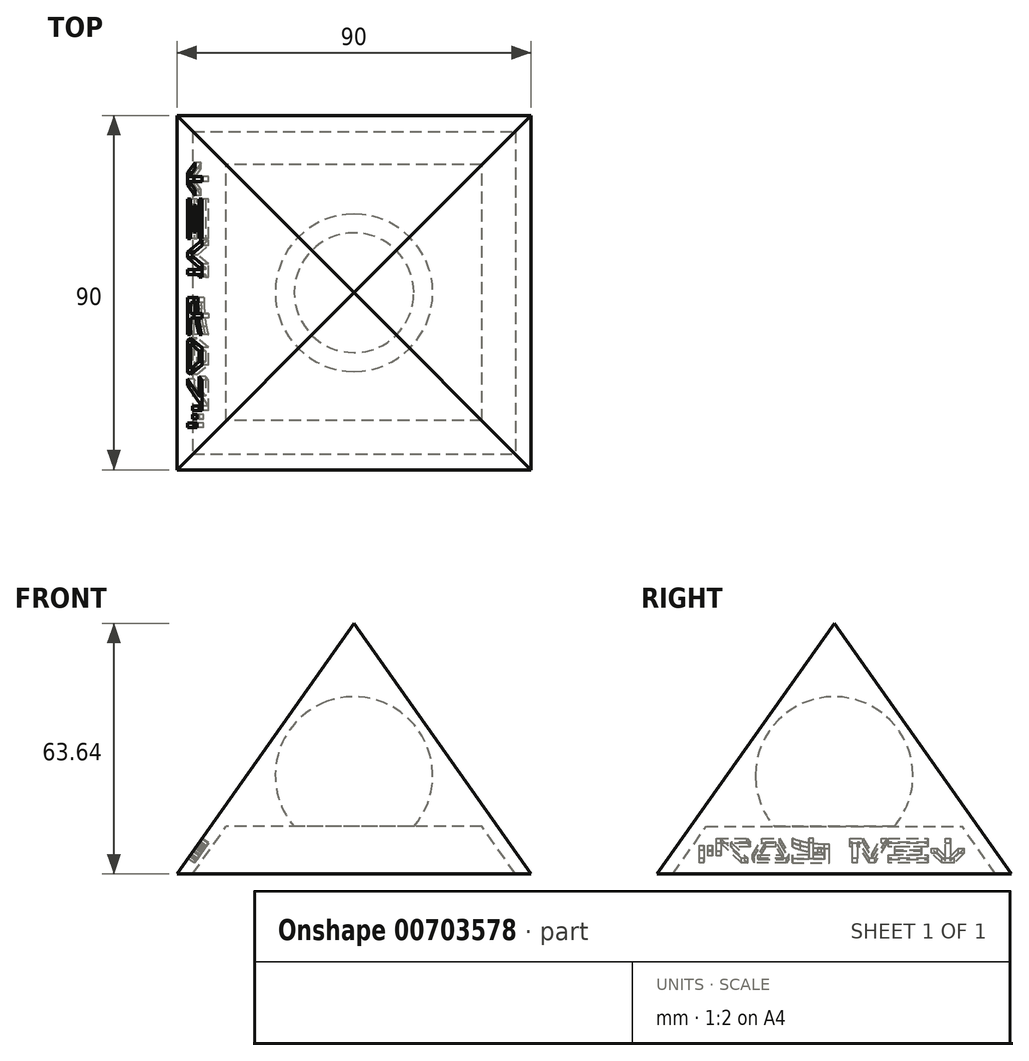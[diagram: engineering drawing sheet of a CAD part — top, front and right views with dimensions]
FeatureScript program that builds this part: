
annotation { "Feature Type Name" : "Feature", "Feature Type Description" : "" }
export const myFeature = defineFeature(function(context is Context, id is Id, definition is map)
    precondition{}
    {
        {
            var Q0;
            Q0=qCreatedBy(makeId("Top.planeOp"),FACE);
            cPlane(context, id + "F0", {"entities" : qUnion([Q0]), "cplaneType" : CPlaneType.OFFSET, "offset" : 63.64 * mm, "width" : 150 * mm, "height" : 150 * mm});
        }
        {
            var Q0;
            Q0=qCreatedBy(id+"F0.planeOp",FACE);
            var sketch = newSketch(context, id + "F1", { "sketchPlane" : qUnion([Q0])});
            skPoint(sketch, "E0", {"position": v(0, 0) * mm});
            skLineSegment(sketch, "E1.bottom", {"start": v(-47.05, 40.97) * mm, "end": v(62.4, 40.97) * mm});
            skLineSegment(sketch, "E1.top", {"start": v(-47.05, -49.65) * mm, "end": v(62.4, -49.65) * mm});
            skLineSegment(sketch, "E1.left", {"start": v(-47.05, 40.97) * mm, "end": v(-47.05, -49.65) * mm});
            skLineSegment(sketch, "E1.right", {"start": v(62.4, 40.97) * mm, "end": v(62.4, -49.65) * mm});
            skSolve(sketch);
        }
        {
            var Q0;
            Q0=qCreatedBy(makeId("Top.planeOp"),FACE);
            var sketch = newSketch(context, id + "F2", { "sketchPlane" : qUnion([Q0])});
            skLineSegment(sketch, "E2.bottom", {"start": v(-45, 45) * mm, "end": v(45, 45) * mm});
            skLineSegment(sketch, "E2.top", {"start": v(-45, -45) * mm, "end": v(45, -45) * mm});
            skLineSegment(sketch, "E2.left", {"start": v(-45, 45) * mm, "end": v(-45, -45) * mm});
            skLineSegment(sketch, "E2.right", {"start": v(45, 45) * mm, "end": v(45, -45) * mm});
            skPoint(sketch, "E3.orphan", {"position": v(-45, 0) * mm});
            skPoint(sketch, "E4.start.orphan", {"position": v(45, 0) * mm});
            skPoint(sketch, "E5.end.orphan", {"position": v(0, -45) * mm});
            skPoint(sketch, "E5.start.orphan", {"position": v(0, 45) * mm});
            skSolve(sketch);
        }
        {
            var Q0;
            Q0=makeQuery(id+"F2.imprint","IMPRINT",FACE,{"disambiguationData":[TD([[makeQuery(id+"F2.imprint","IMPRINT",EDGE,{"derivedFrom":sQuery(id+"F2.wireOp",EDGE,"E2.bottom")}),-1.0]])]});
            var Q1;
            Q1=sQuery(id+"F1.wireOp",VERTEX,"E0");
            loft(context, id + "F3", {"sheetProfilesArray" : [{ "sheetProfileEntities" : qUnion([Q0]) }, { "sheetProfileEntities" : qUnion([Q1]) }]});
        }
        {
            var Q0;
            Q0=qCreatedBy(makeId("Top.planeOp"),FACE);
            cPlane(context, id + "F4", {"entities" : qUnion([Q0]), "cplaneType" : CPlaneType.OFFSET, "offset" : 25 * mm, "width" : 150 * mm, "height" : 150 * mm});
        }
        {
            var Q0;
            Q0=qCreatedBy(makeId("Top.planeOp"),FACE);
            cPlane(context, id + "F5", {"entities" : qUnion([Q0]), "cplaneType" : CPlaneType.OFFSET, "offset" : 58 * mm, "width" : 150 * mm, "height" : 150 * mm});
        }
        {
            var Q0;
            Q0=qCreatedBy(id+"F5.planeOp",FACE);
            var sketch = newSketch(context, id + "F6", { "sketchPlane" : qUnion([Q0])});
            skPoint(sketch, "E6", {"position": v(0, 0) * mm});
            skSolve(sketch);
        }
        {
            var Q0;
            Q0=makeQuery(id+"F2.imprint","IMPRINT",FACE,{"disambiguationData":[TD([[makeQuery(id+"F2.imprint","IMPRINT",EDGE,{"derivedFrom":sQuery(id+"F2.wireOp",EDGE,"E2.bottom")}),-1.0]])]});
            var sketch = newSketch(context, id + "F7", { "sketchPlane" : qUnion([Q0])});
            skLineSegment(sketch, "E7.0", {"start": v(-41, 41) * mm, "end": v(-41, -41) * mm});
            skLineSegment(sketch, "E7.1", {"start": v(-41, 41) * mm, "end": v(41, 41) * mm});
            skLineSegment(sketch, "E7.2", {"start": v(41, 41) * mm, "end": v(41, -41) * mm});
            skLineSegment(sketch, "E7.3", {"start": v(-41, -41) * mm, "end": v(41, -41) * mm});
            skSolve(sketch);
        }
        {
            var Q1;
            Q1=makeQuery(id+"F7.imprint","IMPRINT",FACE,{"disambiguationData":[TD([[makeQuery(id+"F7.imprint","IMPRINT",EDGE,{"derivedFrom":sQuery(id+"F7.wireOp",EDGE,"E7.0")}),1.0]])]});
            var Q2;
            Q2=sQuery(id+"F6.wireOp",VERTEX,"E6");
            loft(context, id + "F8", {"operationType" : NewBodyOperationType.REMOVE, "sheetProfilesArray" : [{ "sheetProfileEntities" : qUnion([Q1]) }, { "sheetProfileEntities" : qUnion([Q2]) }]});
        }
        {
            var Q0;
            Q0=makeQuery(id+"F3.opLoft","SWEPT_FACE",FACE,{"disambiguationData":[OSD([sQuery(id+"F2.wireOp",EDGE,"E2.bottom"),sQuery(id+"F2.wireOp",EDGE,"E2.top"),sQuery(id+"F2.wireOp",EDGE,"E2.left")])]});
            var sketch = newSketch(context, id + "F9", { "sketchPlane" : qUnion([Q0])});
            skLineSegment(sketch, "E8", {"start": v(-30.48, -21.2) * mm, "end": v(-27.31, -21.2) * mm});
            skLineSegment(sketch, "E9", {"start": v(-27.31, -21.2) * mm, "end": v(-24.66, -18.07) * mm});
            skLineSegment(sketch, "E10", {"start": v(-24.66, -18.07) * mm, "end": v(-26.25, -18.07) * mm});
            skLineSegment(sketch, "E11", {"start": v(-26.25, -18.07) * mm, "end": v(-28.3, -20.5) * mm});
            skLineSegment(sketch, "E12", {"start": v(-28.3, -20.5) * mm, "end": v(-28.3, -14.95) * mm});
            skLineSegment(sketch, "E13", {"start": v(-28.3, -14.95) * mm, "end": v(-29.48, -14.95) * mm});
            skLineSegment(sketch, "E14", {"start": v(-29.48, -14.95) * mm, "end": v(-29.48, -20.5) * mm});
            skLineSegment(sketch, "E15", {"start": v(-29.48, -20.5) * mm, "end": v(-31.54, -18.07) * mm});
            skLineSegment(sketch, "E16", {"start": v(-31.54, -18.07) * mm, "end": v(-33.13, -18.07) * mm});
            skLineSegment(sketch, "E17", {"start": v(-33.13, -18.07) * mm, "end": v(-30.48, -21.2) * mm});
            skLineSegment(sketch, "E18", {"start": v(-13.74, -16.13) * mm, "end": v(-13.74, -14.95) * mm});
            skLineSegment(sketch, "E19", {"start": v(-13.74, -14.95) * mm, "end": v(-23.85, -14.95) * mm});
            skLineSegment(sketch, "E20", {"start": v(-23.85, -14.95) * mm, "end": v(-23.85, -16.13) * mm});
            skLineSegment(sketch, "E21", {"start": v(-23.85, -16.13) * mm, "end": v(-13.74, -16.13) * mm});
            skLineSegment(sketch, "E22", {"start": v(-13.74, -21.2) * mm, "end": v(-13.74, -20.01) * mm});
            skLineSegment(sketch, "E23", {"start": v(-13.74, -20.01) * mm, "end": v(-23.85, -20.01) * mm});
            skLineSegment(sketch, "E24", {"start": v(-23.85, -20.01) * mm, "end": v(-23.85, -21.2) * mm});
            skLineSegment(sketch, "E25", {"start": v(-23.85, -21.2) * mm, "end": v(-13.74, -21.2) * mm});
            skLineSegment(sketch, "E26", {"start": v(-15.46, -18.66) * mm, "end": v(-15.46, -17.48) * mm});
            skLineSegment(sketch, "E27", {"start": v(-15.46, -17.48) * mm, "end": v(-22.13, -17.48) * mm});
            skLineSegment(sketch, "E28", {"start": v(-22.13, -17.48) * mm, "end": v(-22.13, -18.66) * mm});
            skLineSegment(sketch, "E29", {"start": v(-22.13, -18.66) * mm, "end": v(-15.46, -18.66) * mm});
            skLineSegment(sketch, "E30", {"start": v(-9.62, -19.72) * mm, "end": v(-11.96, -14.95) * mm});
            skLineSegment(sketch, "E31", {"start": v(-11.96, -14.95) * mm, "end": v(-13.4, -14.95) * mm});
            skLineSegment(sketch, "E32", {"start": v(-13.4, -14.95) * mm, "end": v(-10.33, -21.2) * mm});
            skLineSegment(sketch, "E33", {"start": v(-10.33, -21.2) * mm, "end": v(-8.9, -21.2) * mm});
            skLineSegment(sketch, "E34", {"start": v(-8.9, -21.2) * mm, "end": v(-6.42, -16.13) * mm});
            skLineSegment(sketch, "E35", {"start": v(-6.42, -16.13) * mm, "end": v(-5.84, -16.13) * mm});
            skLineSegment(sketch, "E36", {"start": v(-5.84, -16.13) * mm, "end": v(-5.84, -21.2) * mm});
            skLineSegment(sketch, "E37", {"start": v(-5.84, -21.2) * mm, "end": v(-4.66, -21.2) * mm});
            skLineSegment(sketch, "E38", {"start": v(-4.66, -21.2) * mm, "end": v(-4.66, -16.13) * mm});
            skLineSegment(sketch, "E39", {"start": v(-4.66, -16.13) * mm, "end": v(-3.94, -16.13) * mm});
            skLineSegment(sketch, "E40", {"start": v(-3.94, -16.13) * mm, "end": v(-3.94, -14.95) * mm});
            skLineSegment(sketch, "E41", {"start": v(-3.94, -14.95) * mm, "end": v(-7.28, -14.95) * mm});
            skLineSegment(sketch, "E42", {"start": v(-7.28, -14.95) * mm, "end": v(-9.62, -19.72) * mm});
            skLineSegment(sketch, "E43", {"start": v(2.43, -20.01) * mm, "end": v(5.3, -20.01) * mm});
            skLineSegment(sketch, "E44", {"start": v(5.3, -20.01) * mm, "end": v(5.3, -17.82) * mm});
            skLineSegment(sketch, "E45", {"start": v(2.43, -17.95) * mm, "end": v(2.43, -20.01) * mm});
            skLineSegment(sketch, "E46", {"start": v(5.3, -16.6) * mm, "end": v(5.3, -14.95) * mm});
            skLineSegment(sketch, "E47", {"start": v(5.3, -14.95) * mm, "end": v(6.48, -14.95) * mm});
            skLineSegment(sketch, "E48", {"start": v(6.48, -14.95) * mm, "end": v(6.48, -16.4) * mm});
            skLineSegment(sketch, "E49", {"start": v(10.66, -14.95) * mm, "end": v(10.66, -16.14) * mm});
            skLineSegment(sketch, "E50", {"start": v(6.48, -17.65) * mm, "end": v(6.48, -20.01) * mm});
            skLineSegment(sketch, "E51", {"start": v(6.48, -20.01) * mm, "end": v(10.66, -20.01) * mm});
            skLineSegment(sketch, "E52", {"start": v(10.66, -20.01) * mm, "end": v(10.66, -21.2) * mm});
            skLineSegment(sketch, "E53", {"start": v(10.66, -21.2) * mm, "end": v(1.25, -21.2) * mm});
            skLineSegment(sketch, "E54", {"start": v(1.25, -21.2) * mm, "end": v(1.25, -16.76) * mm});
            skLineSegment(sketch, "E55", {"start": v(1.25, -16.76) * mm, "end": v(2.43, -16.76) * mm});
            skLineSegment(sketch, "E56", {"start": v(12.92, -20.01) * mm, "end": v(14.82, -16.13) * mm});
            skLineSegment(sketch, "E57", {"start": v(14.82, -16.13) * mm, "end": v(17.48, -16.13) * mm});
            skLineSegment(sketch, "E58", {"start": v(17.48, -16.13) * mm, "end": v(19.37, -20.01) * mm});
            skLineSegment(sketch, "E59", {"start": v(19.37, -20.01) * mm, "end": v(12.92, -20.01) * mm});
            skLineSegment(sketch, "E60", {"start": v(20.26, -21.2) * mm, "end": v(20.83, -20.04) * mm});
            skLineSegment(sketch, "E61", {"start": v(20.83, -20.04) * mm, "end": v(18.33, -14.95) * mm});
            skLineSegment(sketch, "E62", {"start": v(18.33, -14.95) * mm, "end": v(13.96, -14.95) * mm});
            skLineSegment(sketch, "E63", {"start": v(13.96, -14.95) * mm, "end": v(11.5, -19.98) * mm});
            skLineSegment(sketch, "E64", {"start": v(11.5, -19.98) * mm, "end": v(12.09, -21.2) * mm});
            skLineSegment(sketch, "E65", {"start": v(12.09, -21.2) * mm, "end": v(20.26, -21.2) * mm});
            skLineSegment(sketch, "E66", {"start": v(23.56, -21.2) * mm, "end": v(28.74, -15.1) * mm});
            skLineSegment(sketch, "E67", {"start": v(28.86, -14.95) * mm, "end": v(22.22, -14.95) * mm});
            skLineSegment(sketch, "E68", {"start": v(22.22, -14.95) * mm, "end": v(21.22, -16.13) * mm});
            skLineSegment(sketch, "E69", {"start": v(21.22, -16.13) * mm, "end": v(26.26, -16.13) * mm});
            skLineSegment(sketch, "E70", {"start": v(26.26, -16.13) * mm, "end": v(21.97, -21.2) * mm});
            skLineSegment(sketch, "E71", {"start": v(21.97, -21.2) * mm, "end": v(23.56, -21.2) * mm});
            skLineSegment(sketch, "E72", {"start": v(29.92, -19) * mm, "end": v(29.92, -14.95) * mm});
            skLineSegment(sketch, "E73", {"start": v(29.92, -14.95) * mm, "end": v(28.74, -14.95) * mm});
            skLineSegment(sketch, "E74", {"start": v(28.74, -15.1) * mm, "end": v(28.74, -19) * mm});
            skLineSegment(sketch, "E75", {"start": v(28.74, -19) * mm, "end": v(29.92, -19) * mm});
            skLineSegment(sketch, "E76", {"start": v(34.22, -21.2) * mm, "end": v(34.22, -17.13) * mm});
            skLineSegment(sketch, "E77", {"start": v(34.22, -17.13) * mm, "end": v(33.04, -17.13) * mm});
            skLineSegment(sketch, "E78", {"start": v(33.04, -17.13) * mm, "end": v(33.04, -21.2) * mm});
            skLineSegment(sketch, "E79", {"start": v(33.04, -21.2) * mm, "end": v(34.22, -21.2) * mm});
            skLineSegment(sketch, "E80", {"start": v(32.07, -19) * mm, "end": v(32.07, -17.13) * mm});
            skLineSegment(sketch, "E81", {"start": v(32.07, -17.13) * mm, "end": v(30.89, -17.13) * mm});
            skLineSegment(sketch, "E82", {"start": v(30.89, -17.13) * mm, "end": v(30.89, -19) * mm});
            skLineSegment(sketch, "E83", {"start": v(30.89, -19) * mm, "end": v(32.07, -19) * mm});
            skFitSpline(sketch, "E84", {"points": [v(5.3, -17.82) * mm, v(5.1, -17.85) * mm, v(4.72, -17.9) * mm, v(4.34, -17.92) * mm, v(4.16, -17.93) * mm]});
            skFitSpline(sketch, "E85", {"points": [v(4.16, -17.93) * mm, v(4, -17.94) * mm, v(3.7, -17.95) * mm, v(3.4, -17.96) * mm, v(3.25, -17.96) * mm]});
            skFitSpline(sketch, "E86", {"points": [v(3.25, -17.96) * mm, v(3.1, -17.97) * mm, v(2.83, -17.97) * mm, v(2.56, -17.96) * mm, v(2.43, -17.95) * mm]});
            skFitSpline(sketch, "E87", {"points": [v(2.43, -16.76) * mm, v(2.56, -16.77) * mm, v(2.82, -16.78) * mm, v(3.1, -16.78) * mm, v(3.23, -16.77) * mm]});
            skFitSpline(sketch, "E88", {"points": [v(3.23, -16.77) * mm, v(3.37, -16.77) * mm, v(3.67, -16.76) * mm, v(3.98, -16.74) * mm, v(4.14, -16.73) * mm]});
            skFitSpline(sketch, "E89", {"points": [v(4.14, -16.73) * mm, v(4.33, -16.71) * mm, v(4.71, -16.68) * mm, v(5.1, -16.63) * mm, v(5.3, -16.6) * mm]});
            skFitSpline(sketch, "E90", {"points": [v(6.48, -16.4) * mm, v(6.81, -16.33) * mm, v(7.5, -16.18) * mm, v(8.18, -15.97) * mm, v(8.52, -15.86) * mm]});
            skFitSpline(sketch, "E91", {"points": [v(8.52, -15.86) * mm, v(8.88, -15.74) * mm, v(9.62, -15.48) * mm, v(10.3, -15.13) * mm, v(10.66, -14.95) * mm]});
            skFitSpline(sketch, "E92", {"points": [v(10.66, -16.14) * mm, v(10.33, -16.3) * mm, v(9.66, -16.64) * mm, v(8.96, -16.92) * mm, v(8.6, -17.05) * mm]});
            skFitSpline(sketch, "E93", {"points": [v(8.6, -17.05) * mm, v(8.25, -17.18) * mm, v(7.56, -17.42) * mm, v(6.84, -17.57) * mm, v(6.48, -17.65) * mm]});
            skSolve(sketch);
        }
        {
            var Q0;
            {var subQ3=sQuery(id+"F9.wireOp",EDGE,"E72");Q0=makeQuery(id+"F9.imprint","IMPRINT",FACE,{"disambiguationData":[TD([[makeQuery(id+"F9.imprint","IMPRINT",EDGE,{"derivedFrom":subQ3}),1.0]])]});}
            var Q1;
            Q1=makeQuery(id+"F9.imprint","IMPRINT",FACE,{"disambiguationData":[TD([[makeQuery(id+"F9.imprint","IMPRINT",EDGE,{"derivedFrom":sQuery(id+"F9.wireOp",EDGE,"E80")}),1.0]])]});
            var Q2;
            Q2=makeQuery(id+"F9.imprint","IMPRINT",FACE,{"disambiguationData":[TD([[makeQuery(id+"F9.imprint","IMPRINT",EDGE,{"derivedFrom":sQuery(id+"F9.wireOp",EDGE,"E76")}),1.0]])]});
            var Q3;
            Q3=makeQuery(id+"F9.imprint","IMPRINT",FACE,{"disambiguationData":[TD([[makeQuery(id+"F9.imprint","IMPRINT",EDGE,{"derivedFrom":sQuery(id+"F9.wireOp",EDGE,"E56")}),1.0]])]});
            var Q4;
            Q4=makeQuery(id+"F9.imprint","IMPRINT",FACE,{"disambiguationData":[TD([[makeQuery(id+"F9.imprint","IMPRINT",EDGE,{"derivedFrom":sQuery(id+"F9.wireOp",EDGE,"E43")}),-1.0]])]});
            var Q5;
            Q5=makeQuery(id+"F9.imprint","IMPRINT",FACE,{"disambiguationData":[TD([[makeQuery(id+"F9.imprint","IMPRINT",EDGE,{"derivedFrom":sQuery(id+"F9.wireOp",EDGE,"E30")}),1.0]])]});
            var Q6;
            Q6=makeQuery(id+"F9.imprint","IMPRINT",FACE,{"disambiguationData":[TD([[makeQuery(id+"F9.imprint","IMPRINT",EDGE,{"derivedFrom":sQuery(id+"F9.wireOp",EDGE,"E18")}),1.0]])]});
            var Q7;
            Q7=makeQuery(id+"F9.imprint","IMPRINT",FACE,{"disambiguationData":[TD([[makeQuery(id+"F9.imprint","IMPRINT",EDGE,{"derivedFrom":sQuery(id+"F9.wireOp",EDGE,"E26")}),1.0]])]});
            var Q8;
            Q8=makeQuery(id+"F9.imprint","IMPRINT",FACE,{"disambiguationData":[TD([[makeQuery(id+"F9.imprint","IMPRINT",EDGE,{"derivedFrom":sQuery(id+"F9.wireOp",EDGE,"E22")}),1.0]])]});
            var Q9;
            Q9=makeQuery(id+"F9.imprint","IMPRINT",FACE,{"disambiguationData":[TD([[makeQuery(id+"F9.imprint","IMPRINT",EDGE,{"derivedFrom":sQuery(id+"F9.wireOp",EDGE,"E8")}),1.0]])]});
            extrude(context, id + "F10", {"entities" : qUnion([Q0, Q1, Q2, Q3, Q4, Q5, Q6, Q7, Q8, Q9]), "operationType" : NewBodyOperationType.REMOVE, "oppositeDirection" : true, "depth" : 2 * mm, "offsetDistance" : 25 * mm});
        }
        {
            var Q0;
            Q0=qCreatedBy(id+"F4.planeOp",FACE);
            var sketch = newSketch(context, id + "F11", { "sketchPlane" : qUnion([Q0])});
            skPoint(sketch, "E94", {"position": v(0, 0) * mm});
            skCircle(sketch, "E95", {"center": v(0, 0) * mm, "radius": 20 * mm});
            skLineSegment(sketch, "E96", {"start": v(0, -20) * mm, "end": v(0, 20) * mm});
            skSolve(sketch);
        }
        {
            var Q0;
            Q0=qCreatedBy(makeId("Top.planeOp"),FACE);
            cPlane(context, id + "F12", {"entities" : qUnion([Q0]), "cplaneType" : CPlaneType.OFFSET, "offset" : 12 * mm, "width" : 150 * mm, "height" : 150 * mm});
        }
        {
            var Q0;
            Q0=qCreatedBy(id+"F12.planeOp",FACE);
            var sketch = newSketch(context, id + "F13", { "sketchPlane" : qUnion([Q0])});
            skLineSegment(sketch, "E97.bottom", {"start": v(-33, -33) * mm, "end": v(33, -33) * mm});
            skLineSegment(sketch, "E97.top", {"start": v(-33, 33) * mm, "end": v(33, 33) * mm});
            skLineSegment(sketch, "E97.left", {"start": v(-33, -33) * mm, "end": v(-33, 33) * mm});
            skLineSegment(sketch, "E97.right", {"start": v(33, -33) * mm, "end": v(33, 33) * mm});
            skLineSegment(sketch, "E98", {"start": v(-33, 0) * mm, "end": v(33, 0) * mm, "construction": true});
            skLineSegment(sketch, "E99", {"start": v(0, -33) * mm, "end": v(0, 33) * mm, "construction": true});
            skSolve(sketch);
        }
        {
            var Q1;
            Q1=sQuery(id+"F6.wireOp",VERTEX,"E6");
            var Q2;
            Q2=makeQuery(id+"F13.imprint","IMPRINT",FACE,{"disambiguationData":[TD([[makeQuery(id+"F13.imprint","IMPRINT",EDGE,{"derivedFrom":sQuery(id+"F13.wireOp",EDGE,"E97.bottom")}),1.0]])]});
            loft(context, id + "F14", {"operationType" : NewBodyOperationType.ADD, "sheetProfilesArray" : [{ "sheetProfileEntities" : qUnion([Q1]) }, { "sheetProfileEntities" : qUnion([Q2]) }]});
        }
        {
            var Q0;
            {var subQ0=sQuery(id+"F11.wireOp",EDGE,"E96");Q0=makeQuery(id+"F11.imprint","IMPRINT",FACE,{"disambiguationData":[TD([[makeQuery(id+"F11.imprint","IMPRINT",EDGE,{"derivedFrom":subQ0}),1.0]])]});}
            var Q1;
            Q1=sQuery(id+"F11.wireOp",EDGE,"E96");
            revolve(context, id + "F15", {"operationType" : NewBodyOperationType.REMOVE, "surfaceOperationType" : NewSurfaceOperationType.NEW, "entities" : qUnion([Q0]), "axis" : qUnion([Q1]), "revolveType" : RevolveType.FULL, "oppositeDirection" : true});
        }
    });
